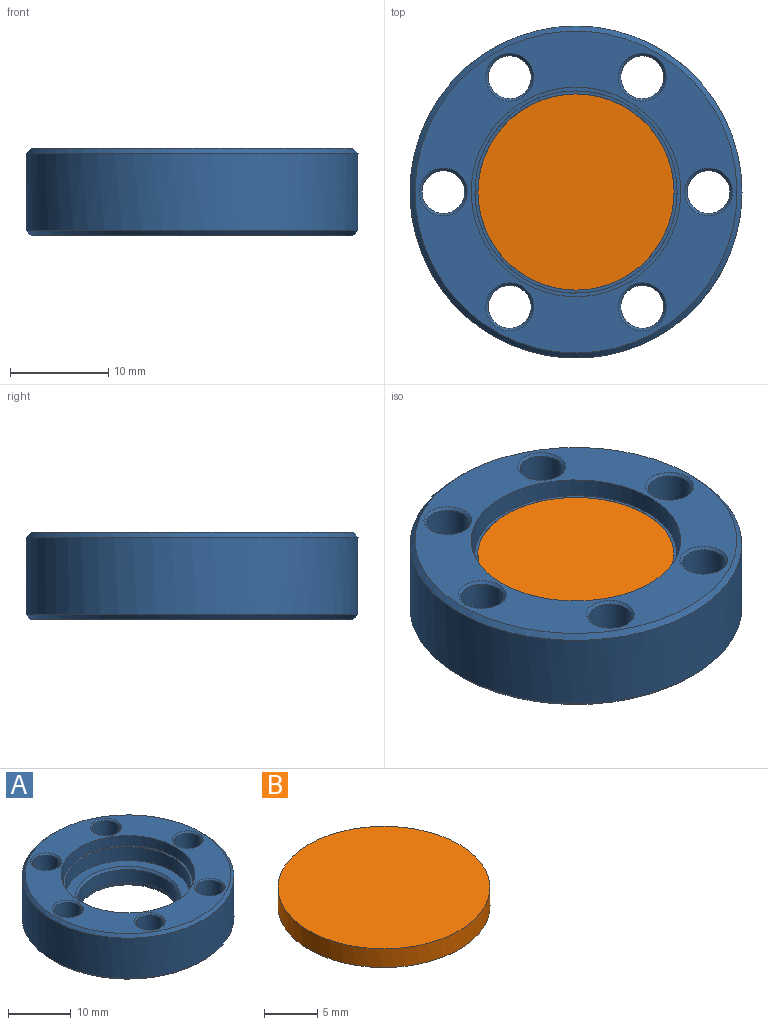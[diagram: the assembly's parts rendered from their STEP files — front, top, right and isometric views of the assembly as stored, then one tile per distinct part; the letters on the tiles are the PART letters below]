
ASSEMBLY  parts=2 mates=1
PART A: 42 faces, bbox 33.8x33.8x8.9 mm
  f0: plane 32.77x32.77mm, normal (0,0,-1), area 370.2mm2, adj f3,f6,f15,f19,f21,f31,f32,f40
  f1: plane 20.57x20.57mm, normal (0,0,1), area 19.4mm2, adj f25,f39
  f2: plane 18.29x18.29mm, normal (0,0,-1), area 61.6mm2, adj f33,f34
  f3: cone r=16.38mm half-angle=45deg, axis (0,0,1), area 75.1mm2, adj f0,f9
  f4: cone r=16.89mm half-angle=45deg, axis (0,0,-1), area 75.1mm2, adj f9,f12
  f5: cylinder r=9.02mm len=18.03mm, axis (0,0,1), area 64.8mm2, adj f28,f41
  f6: cone r=2.44mm half-angle=45deg, axis (0,0,-1), area 5.2mm2, adj f0,f16
  f7: cone r=9.14mm half-angle=70deg, axis (0,0,1), area 104.6mm2, adj f31,f34
  f8: cone r=2.18mm half-angle=45deg, axis (0,0,1), area 5.2mm2, adj f12,f18
  f9: cylinder r=16.89mm len=33.78mm, axis (0,0,1), area 833mm2, adj f3,f4
  f10: torus R=10.03mm, axis (0,0,-1), area 25.6mm2, adj f25,f29
  f11: cylinder r=10.67mm len=21.34mm, axis (0,0,1), area 321.8mm2, adj f12,f41
  f12: plane 32.77x32.77mm, normal (0,0,1), area 373.6mm2, adj f4,f8,f11,f13,f22,f23,f35,f36
  f13: cone r=2.18mm half-angle=45deg, axis (0,0,1), area 5.2mm2, adj f12,f14
  f14: cylinder r=2.18mm len=8.36mm, axis (0,0,-1), area 114.7mm2, adj f13,f15
  f15: cone r=2.44mm half-angle=45deg, axis (0,0,-1), area 5.2mm2, adj f0,f14
  f16: cylinder r=2.18mm len=8.36mm, axis (0,0,-1), area 114.7mm2, adj f6,f36
  f17: cylinder r=8.32mm len=16.64mm, axis (0,0,1), area 87.5mm2, adj f28,f29
  f18: cylinder r=2.18mm len=8.36mm, axis (0,0,-1), area 114.7mm2, adj f8,f40
  f19: cone r=2.44mm half-angle=45deg, axis (0,0,-1), area 5.2mm2, adj f0,f24
  f20: cylinder r=2.18mm len=8.36mm, axis (0,0,-1), area 114.7mm2, adj f21,f23
  f21: cone r=2.44mm half-angle=45deg, axis (0,0,-1), area 5.2mm2, adj f0,f20
  f22: cone r=2.18mm half-angle=45deg, axis (0,0,1), area 5.2mm2, adj f12,f24
  f23: cone r=2.18mm half-angle=45deg, axis (0,0,1), area 5.2mm2, adj f12,f20
  f24: cylinder r=2.18mm len=8.36mm, axis (0,0,-1), area 114.7mm2, adj f19,f22
  f25: cylinder r=10.29mm len=20.57mm, axis (0,0,1), area 175.7mm2, adj f1,f10
  f26: cone r=8.39mm half-angle=45deg, axis (0,0,1), area 27.8mm2, adj f27,f30
  f27: cylinder r=8.01mm len=16.03mm, axis (0,0,1), area 124.1mm2, adj f26,f38
  f28: cone r=9.02mm half-angle=60deg, axis (0,0,1), area 43.9mm2, adj f5,f17
  f29: plane 20.07x20.07mm, normal (0,0,-1), area 98.8mm2, adj f10,f17
  f30: plane 19.96x19.96mm, normal (0,0,1), area 91.7mm2, adj f26,f39
  f31: cylinder r=10.72mm len=21.44mm, axis (0,0,1), area 81.4mm2, adj f0,f7
  f32: cone r=2.44mm half-angle=45deg, axis (0,0,-1), area 5.2mm2, adj f0,f37
  f33: cylinder r=8mm len=16mm, axis (0,0,1), area 25.5mm2, adj f2,f38
  f34: cylinder r=9.14mm len=18.29mm, axis (0,0,1), area 29.2mm2, adj f2,f7
  f35: cone r=2.18mm half-angle=45deg, axis (0,0,1), area 5.2mm2, adj f12,f37
  f36: cone r=2.18mm half-angle=45deg, axis (0,0,1), area 5.2mm2, adj f12,f16
  f37: cylinder r=2.18mm len=8.36mm, axis (0,0,-1), area 114.7mm2, adj f32,f35
  f38: plane 16.03x16.03mm, normal (0,0,1), area 0.6mm2, adj f27,f33
  f39: cylinder r=9.98mm len=19.96mm, axis (0,0,1), area 167.3mm2, adj f1,f30
  f40: cone r=2.44mm half-angle=45deg, axis (0,0,-1), area 5.2mm2, adj f0,f18
  f41: plane 21.34x21.34mm, normal (0,0,1), area 102.1mm2, adj f5,f11
PART B: 3 faces, bbox 20x20x2.2 mm
  f0: plane 19.96x19.96mm, normal (0,0,1), area 313mm2, adj f1
  f1: cylinder r=9.98mm len=19.96mm, axis (0,0,-1), area 135.4mm2, adj f0,f2
  f2: plane 19.96x19.96mm, normal (0,0,-1), area 313mm2, adj f1
PLACE A at identity
PLACE B at identity
MATE fastened B.f1 <-> A.f3  axis (0,0,1) through (0,0,7.16)mm
